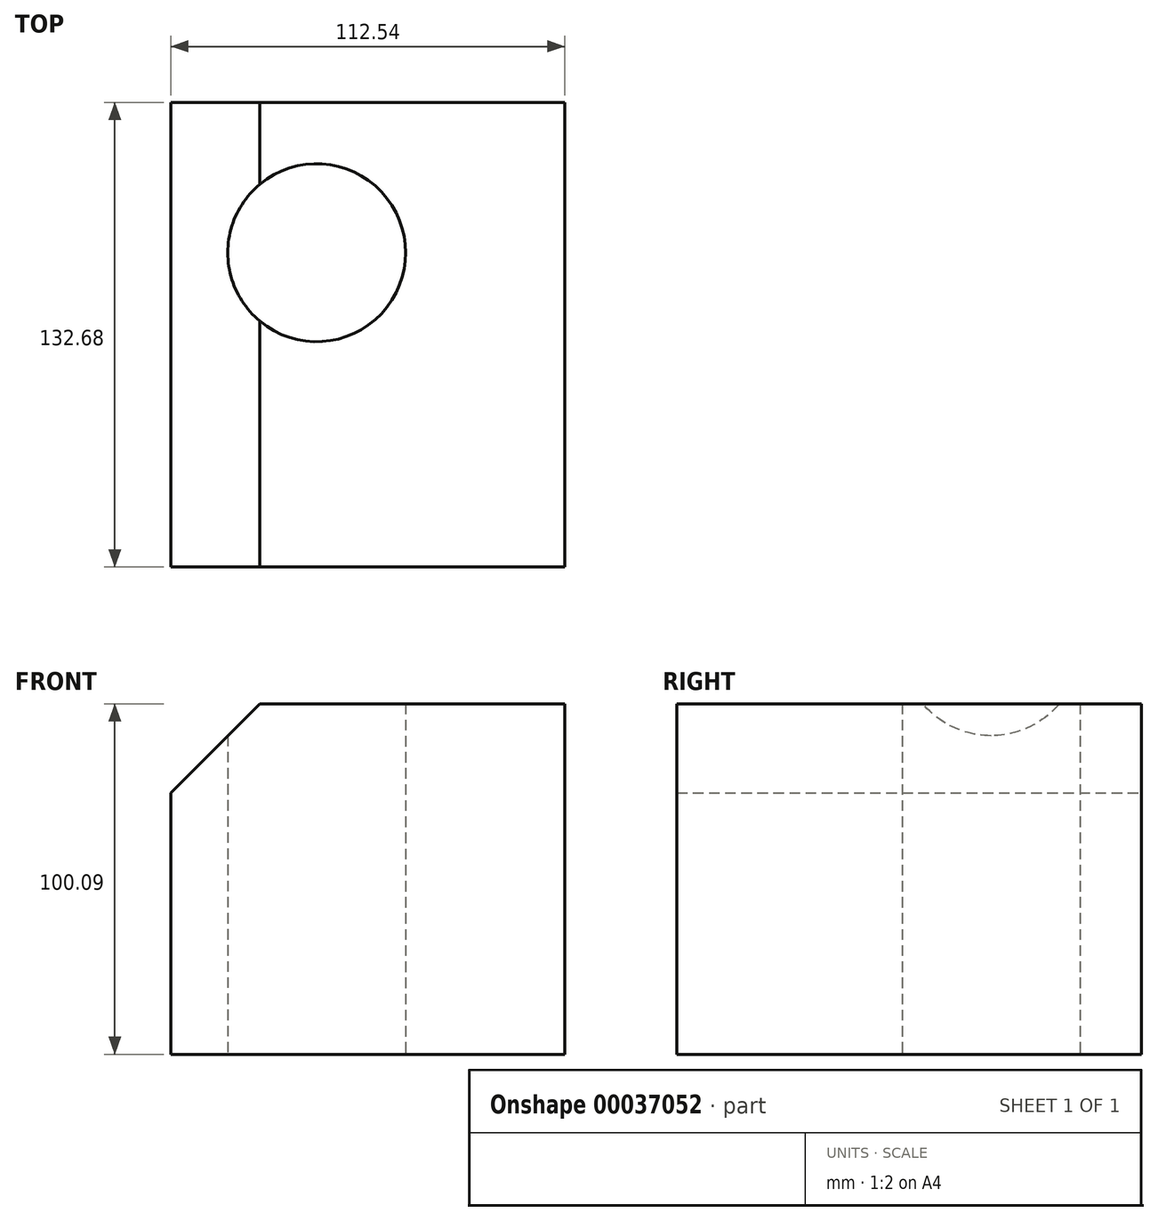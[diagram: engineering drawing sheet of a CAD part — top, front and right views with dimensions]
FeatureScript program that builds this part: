
annotation { "Feature Type Name" : "Feature", "Feature Type Description" : "" }
export const myFeature = defineFeature(function(context is Context, id is Id, definition is map)
    precondition{}
    {
        {
            var Q0;
            Q0=qCreatedBy(makeId("Front.planeOp"),FACE);
            var sketch = newSketch(context, id + "F0", { "sketchPlane" : qUnion([Q0])});
            skLineSegment(sketch, "E0.bottom", {"start": v(-100.3, 56.09) * mm, "end": v(12.23, 56.09) * mm});
            skLineSegment(sketch, "E0.top", {"start": v(-100.3, -44) * mm, "end": v(12.23, -44) * mm});
            skLineSegment(sketch, "E0.left", {"start": v(-100.3, 56.09) * mm, "end": v(-100.3, -44) * mm});
            skLineSegment(sketch, "E0.right", {"start": v(12.23, 56.09) * mm, "end": v(12.23, -44) * mm});
            skSolve(sketch);
        }
        {
            var Q0;
            Q0=makeQuery(id+"F0.imprint","IMPRINT",FACE,{"disambiguationData":[TD([[makeQuery(id+"F0.imprint","IMPRINT",EDGE,{"derivedFrom":sQuery(id+"F0.wireOp",EDGE,"E0.bottom")}),-1.0]])]});
            extrude(context, id + "F1", {"entities" : qUnion([Q0]), "depth" : 132.68 * mm});
        }
        {
            var Q0;
            Q0=makeQuery(id+"F1.opExtrude","SWEPT_FACE",FACE,{"disambiguationData":[OSD([sQuery(id+"F0.wireOp",EDGE,"E0.top")])]});
            var sketch = newSketch(context, id + "F2", { "sketchPlane" : qUnion([Q0])});
            skPoint(sketch, "E1", {"position": v(-58.66, 42.93) * mm});
            skSolve(sketch);
        }
        {
            var Q0;
            Q0=sQuery(id+"F2.wireOp",VERTEX,"E1");
            var Q1;
            Q1=makeQuery(id+"F1.opExtrude","SWEPT_BODY",BODY,{"disambiguationData":[OSD([sQuery(id+"F0.wireOp",EDGE,"E0.bottom"),sQuery(id+"F0.wireOp",EDGE,"E0.top"),sQuery(id+"F0.wireOp",EDGE,"E0.left"),sQuery(id+"F0.wireOp",EDGE,"E0.right")])]});
            hole(context, id + "F3", {"style" : HoleStyle.SIMPLE, "holeDiameter" : 50.8 * mm, "endStyle" : HoleEndStyle.THROUGH, "locations" : qUnion([Q0]), "scope" : qUnion([Q1])});
        }
        {
            var Q0;
            Q0=makeQuery(id+"F1.opExtrude","SWEPT_EDGE",EDGE,{"disambiguationData":[OSD([sQuery(id+"F0.wireOp",EDGE,"E0.bottom"),sQuery(id+"F0.wireOp",EDGE,"E0.left")])]});
            chamfer(context, id + "F4", {"entities" : qUnion([Q0]), "width" : 25.4 * mm, "tangentPropagation" : true});
        }
    });
